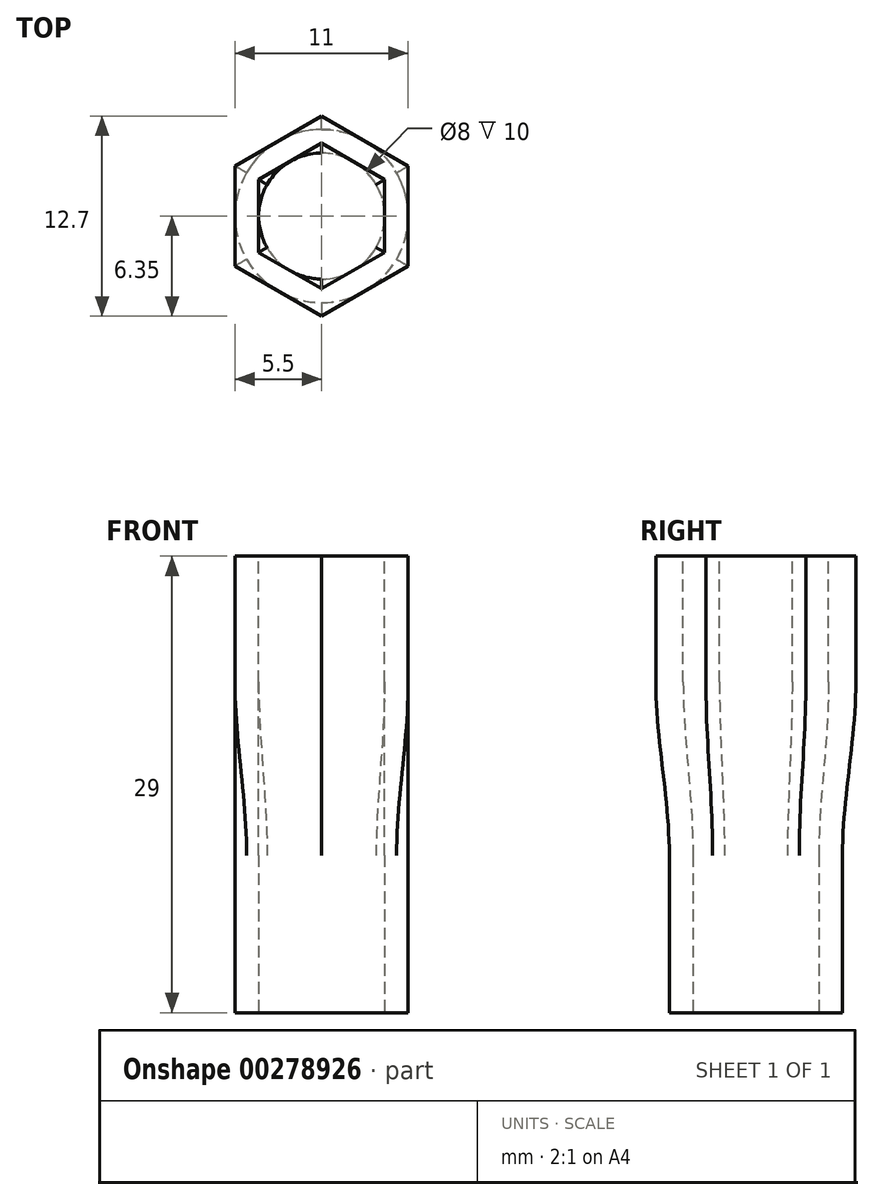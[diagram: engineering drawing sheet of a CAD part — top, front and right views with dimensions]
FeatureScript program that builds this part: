
annotation { "Feature Type Name" : "Feature", "Feature Type Description" : "" }
export const myFeature = defineFeature(function(context is Context, id is Id, definition is map)
    precondition{}
    {
        {
            assignVariable(context, id + "F0", {"name" : "ShaftLength", "anyValue" : 8});
        }
        {
            assignVariable(context, id + "F1", {"name" : "SpindleLength", "anyValue" : 10});
        }
        {
            assignVariable(context, id + "F2", {"name" : "TotalLength", "anyValue" : 29});
        }
        {
            var Q0;
            Q0=qCreatedBy(makeId("Top.planeOp"),FACE);
            var sketch = newSketch(context, id + "F3", { "sketchPlane" : qUnion([Q0])});
            skCircle(sketch, "E0", {"center": v(0, 0) * mm, "radius": 5.5 * mm});
            skSolve(sketch);
        }
        {
            var Q0;
            Q0=makeQuery(id+"F3.imprint","IMPRINT",FACE,{"disambiguationData":[TD([[makeQuery(id+"F3.imprint","IMPRINT",EDGE,{"derivedFrom":sQuery(id+"F3.wireOp",EDGE,"hNRPjWRJ-6WuB-WL1z-FBUq-CvtZZifd5Yuq")}),-1.0]])]});
            var Q1;
            Q1=makeQuery(id+"F3.imprint","IMPRINT",FACE,{"disambiguationData":[TD([[makeQuery(id+"F3.imprint","IMPRINT",EDGE,{"derivedFrom":sQuery(id+"F3.wireOp",EDGE,"E0")}),1.0]])]});
            extrude(context, id + "F4", {"entities" : qUnion([Q0, Q1]), "depth" : (getVariable(context, 'SpindleLength')) * mm});
        }
        {
            var Q0;
            Q0=qCreatedBy(makeId("Top.planeOp"),FACE);
            cPlane(context, id + "F5", {"entities" : qUnion([Q0]), "cplaneType" : CPlaneType.OFFSET, "offset" : (getVariable(context, 'TotalLength')) * mm, "width" : 150 * mm, "height" : 150 * mm});
        }
        {
            var Q0;
            Q0=qCreatedBy(id+"F5.planeOp",FACE);
            var sketch = newSketch(context, id + "F6", { "sketchPlane" : qUnion([Q0])});
            skCircle(sketch, "E1.cCircle", {"center": v(0, 0) * mm, "radius": 5.5 * mm, "construction": true});
            skLineSegment(sketch, "E1.0", {"start": v(5.5, 3.18) * mm, "end": v(5.5, -3.18) * mm});
            skLineSegment(sketch, "E1.1", {"start": v(5.5, -3.18) * mm, "end": v(0, -6.35) * mm});
            skLineSegment(sketch, "E1.2", {"start": v(0, -6.35) * mm, "end": v(-5.5, -3.18) * mm});
            skLineSegment(sketch, "E1.3", {"start": v(-5.5, -3.18) * mm, "end": v(-5.5, 3.18) * mm});
            skLineSegment(sketch, "E1.4", {"start": v(-5.5, 3.18) * mm, "end": v(0, 6.35) * mm});
            skLineSegment(sketch, "E1.5", {"start": v(0, 6.35) * mm, "end": v(5.5, 3.18) * mm});
            skPoint(sketch, "E1.0.midPoint", {"position": v(5.5, 0) * mm});
            skSolve(sketch);
        }
        {
            var Q0;
            Q0=makeQuery(id+"F6.imprint","IMPRINT",FACE,{"disambiguationData":[TD([[makeQuery(id+"F6.imprint","IMPRINT",EDGE,{"derivedFrom":sQuery(id+"F6.wireOp",EDGE,"E1.0")}),-1.0]])]});
            extrude(context, id + "F7", {"entities" : qUnion([Q0]), "oppositeDirection" : true, "depth" : (getVariable(context, 'ShaftLength')) * mm});
        }
        {
            var Q1;
            Q1=makeQuery(id+"F4.opExtrude","CAP_FACE",FACE,{"disambiguationData":[OSD([sQuery(id+"F3.wireOp",EDGE,"E0")])],"isStart":false});
            var Q2;
            Q2=makeQuery(id+"F7.opExtrude","CAP_FACE",FACE,{"disambiguationData":[OSD([sQuery(id+"F6.wireOp",EDGE,"E1.0"),sQuery(id+"F6.wireOp",EDGE,"E1.1"),sQuery(id+"F6.wireOp",EDGE,"E1.2"),sQuery(id+"F6.wireOp",EDGE,"E1.3"),sQuery(id+"F6.wireOp",EDGE,"E1.4"),sQuery(id+"F6.wireOp",EDGE,"E1.5")])],"isStart":false});
            loft(context, id + "F8", {"operationType" : NewBodyOperationType.ADD, "startCondition" : LoftEndDerivativeType.NORMAL_TO_PROFILE, "startMagnitude" : 1, "endCondition" : LoftEndDerivativeType.NORMAL_TO_PROFILE, "endMagnitude" : 1, "sheetProfilesArray" : [{ "sheetProfileEntities" : qUnion([Q1]) }, { "sheetProfileEntities" : qUnion([Q2]) }]});
        }
        {
            var Q0;
            Q0=makeQuery(id+"F7.opExtrude","CAP_FACE",FACE,{"disambiguationData":[OSD([sQuery(id+"F6.wireOp",EDGE,"E1.0"),sQuery(id+"F6.wireOp",EDGE,"E1.1"),sQuery(id+"F6.wireOp",EDGE,"E1.2"),sQuery(id+"F6.wireOp",EDGE,"E1.3"),sQuery(id+"F6.wireOp",EDGE,"E1.4"),sQuery(id+"F6.wireOp",EDGE,"E1.5")])],"isStart":true});
            var sketch = newSketch(context, id + "F9", { "sketchPlane" : qUnion([Q0])});
            skCircle(sketch, "E2.cCircle", {"center": v(0, 0) * mm, "radius": 4 * mm, "construction": true});
            skLineSegment(sketch, "E2.0", {"start": v(4, 2.3) * mm, "end": v(4, -2.3) * mm});
            skLineSegment(sketch, "E2.1", {"start": v(4, -2.3) * mm, "end": v(0, -4.62) * mm});
            skLineSegment(sketch, "E2.2", {"start": v(0, -4.62) * mm, "end": v(-4, -2.3) * mm});
            skLineSegment(sketch, "E2.3", {"start": v(-4, -2.3) * mm, "end": v(-4, 2.3) * mm});
            skLineSegment(sketch, "E2.4", {"start": v(-4, 2.3) * mm, "end": v(0, 4.62) * mm});
            skLineSegment(sketch, "E2.5", {"start": v(0, 4.62) * mm, "end": v(4, 2.3) * mm});
            skPoint(sketch, "E2.0.midPoint", {"position": v(4, 0) * mm});
            skSolve(sketch);
        }
        {
            var Q0;
            Q0=makeQuery(id+"F9.imprint","IMPRINT",FACE,{"disambiguationData":[TD([[makeQuery(id+"F9.imprint","IMPRINT",EDGE,{"derivedFrom":sQuery(id+"F9.wireOp",EDGE,"E2.0")}),-1.0]])]});
            extrude(context, id + "F10", {"entities" : qUnion([Q0]), "operationType" : NewBodyOperationType.REMOVE, "oppositeDirection" : true, "depth" : (getVariable(context, 'ShaftLength')) * mm});
        }
        {
            var Q0;
            Q0=makeQuery(id+"F4.opExtrude","CAP_FACE",FACE,{"disambiguationData":[OSD([sQuery(id+"F3.wireOp",EDGE,"E0")])],"isStart":true});
            var sketch = newSketch(context, id + "F11", { "sketchPlane" : qUnion([Q0])});
            skCircle(sketch, "E3", {"center": v(0, 0) * mm, "radius": 4 * mm});
            skSolve(sketch);
        }
        {
            var Q0;
            Q0=makeQuery(id+"F11.imprint","IMPRINT",FACE,{"disambiguationData":[TD([[makeQuery(id+"F11.imprint","IMPRINT",EDGE,{"derivedFrom":sQuery(id+"F11.wireOp",EDGE,"E3")}),1.0]])]});
            extrude(context, id + "F12", {"entities" : qUnion([Q0]), "operationType" : NewBodyOperationType.REMOVE, "oppositeDirection" : true, "depth" : (getVariable(context, 'SpindleLength')) * mm});
        }
        {
            var Q1;
            Q1=makeQuery(id+"F10.boolean.opBoolean","COPY",FACE,{"derivedFrom":makeQuery(id+"F10.opExtrude","CAP_FACE",FACE,{"disambiguationData":[OSD([sQuery(id+"F9.wireOp",EDGE,"E2.0"),sQuery(id+"F9.wireOp",EDGE,"E2.1"),sQuery(id+"F9.wireOp",EDGE,"E2.2"),sQuery(id+"F9.wireOp",EDGE,"E2.3"),sQuery(id+"F9.wireOp",EDGE,"E2.4"),sQuery(id+"F9.wireOp",EDGE,"E2.5")])],"isStart":false})});
            var Q2;
            Q2=makeQuery(id+"F12.boolean.opBoolean","COPY",FACE,{"derivedFrom":makeQuery(id+"F12.opExtrude","CAP_FACE",FACE,{"disambiguationData":[OSD([sQuery(id+"F11.wireOp",EDGE,"E3")])],"isStart":false})});
            loft(context, id + "F13", {"operationType" : NewBodyOperationType.REMOVE, "startCondition" : LoftEndDerivativeType.NORMAL_TO_PROFILE, "startMagnitude" : 1, "endCondition" : LoftEndDerivativeType.NORMAL_TO_PROFILE, "endMagnitude" : 1, "sheetProfilesArray" : [{ "sheetProfileEntities" : qUnion([Q1]) }, { "sheetProfileEntities" : qUnion([Q2]) }]});
        }
    });
